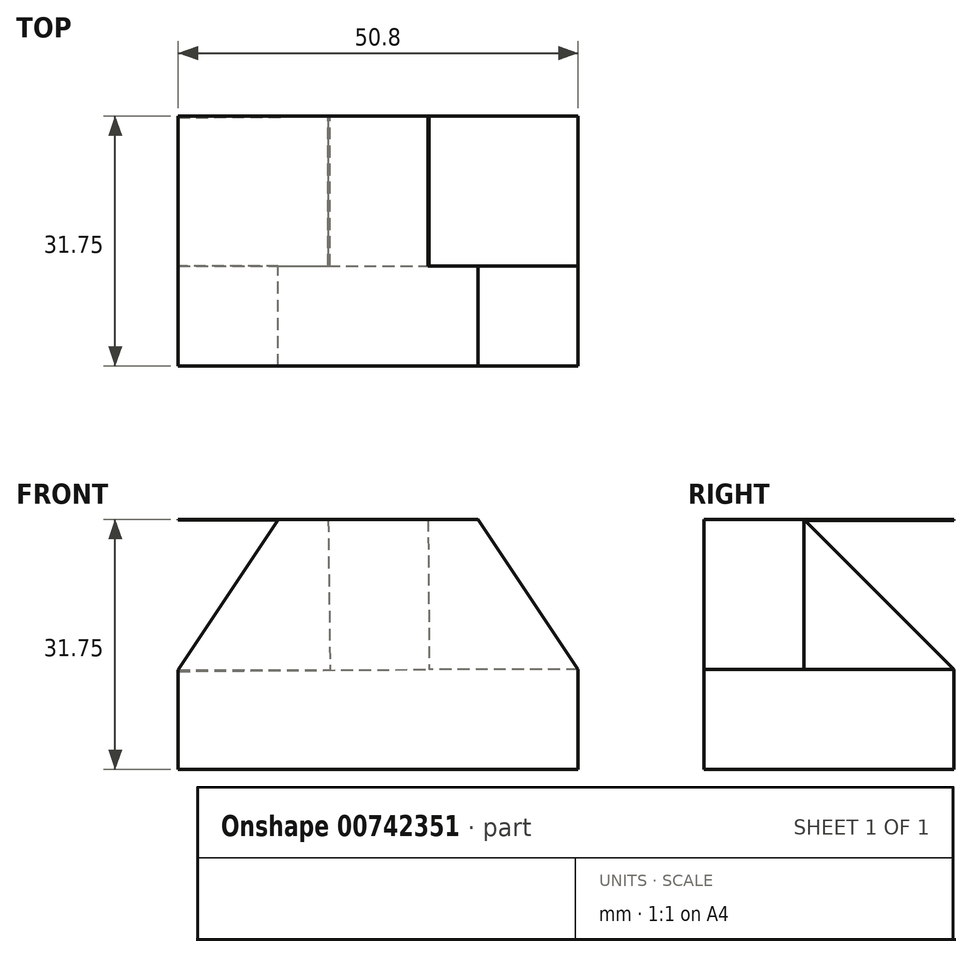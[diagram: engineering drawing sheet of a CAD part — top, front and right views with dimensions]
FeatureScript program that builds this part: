
annotation { "Feature Type Name" : "Feature", "Feature Type Description" : "" }
export const myFeature = defineFeature(function(context is Context, id is Id, definition is map)
    precondition{}
    {
        {
            var Q0;
            Q0=qCreatedBy(makeId("Front.planeOp"),FACE);
            var sketch = newSketch(context, id + "F0", { "sketchPlane" : qUnion([Q0])});
            skLineSegment(sketch, "E0", {"start": v(0, 0) * mm, "end": v(50.8, 0) * mm});
            skLineSegment(sketch, "E1", {"start": v(50.8, 0) * mm, "end": v(50.8, 31.75) * mm});
            skLineSegment(sketch, "E2", {"start": v(50.8, 31.75) * mm, "end": v(0, 31.75) * mm});
            skLineSegment(sketch, "E3", {"start": v(0, 31.75) * mm, "end": v(0, 0) * mm});
            skSolve(sketch);
        }
        {
            var Q0;
            Q0 = qSketchRegion(id + "F0", true);
            extrude(context, id + "F1", {"entities" : qUnion([Q0]), "depth" : 31.75 * mm, "offsetDistance" : 25.4 * mm});
        }
        {
            var Q0;
            Q0=qCreatedBy(makeId("Front.planeOp"),FACE);
            var sketch = newSketch(context, id + "F2", { "sketchPlane" : qUnion([Q0])});
            skLineSegment(sketch, "E4", {"start": v(50.83, 12.7) * mm, "end": v(31.89, 12.7) * mm});
            skLineSegment(sketch, "E5", {"start": v(31.89, 12.7) * mm, "end": v(31.75, 31.75) * mm});
            skLineSegment(sketch, "E6", {"start": v(31.75, 31.75) * mm, "end": v(50.8, 31.75) * mm});
            skLineSegment(sketch, "E7", {"start": v(50.8, 31.75) * mm, "end": v(50.83, 12.7) * mm});
            skLineSegment(sketch, "E8", {"start": v(0, 12.66) * mm, "end": v(19.3, 12.66) * mm});
            skLineSegment(sketch, "E9", {"start": v(0, 12.66) * mm, "end": v(0, 31.71) * mm});
            skLineSegment(sketch, "E10", {"start": v(0, 31.71) * mm, "end": v(19.05, 31.71) * mm});
            skLineSegment(sketch, "E11", {"start": v(19.05, 31.71) * mm, "end": v(19.3, 12.66) * mm});
            skSolve(sketch);
        }
        {
            var Q0;
            Q0 = qSketchRegion(id + "F2", true);
            extrude(context, id + "F3", {"entities" : qUnion([Q0]), "operationType" : NewBodyOperationType.REMOVE, "depth" : 19.05 * mm, "offsetDistance" : 25.4 * mm});
        }
        {
            var Q0;
            Q0=makeQuery(id+"F3.boolean.opBoolean","COPY",FACE,{"derivedFrom":makeQuery(id+"F3.opExtrude","CAP_FACE",FACE,{"disambiguationData":[OSD([sQuery(id+"F2.wireOp",EDGE,"E8"),sQuery(id+"F2.wireOp",EDGE,"E9"),sQuery(id+"F2.wireOp",EDGE,"E10"),sQuery(id+"F2.wireOp",EDGE,"E11")])],"isStart":false})});
            var sketch = newSketch(context, id + "F4", { "sketchPlane" : qUnion([Q0])});
            skLineSegment(sketch, "E12", {"start": v(-12.7, 31.71) * mm, "end": v(0, 12.66) * mm});
            skLineSegment(sketch, "E13", {"start": v(0, 12.66) * mm, "end": v(0, 31.71) * mm});
            skLineSegment(sketch, "E14", {"start": v(0, 31.71) * mm, "end": v(-12.7, 31.71) * mm});
            skSolve(sketch);
        }
        {
            var Q0;
            Q0 = qSketchRegion(id + "F4", true);
            extrude(context, id + "F5", {"entities" : qUnion([Q0]), "operationType" : NewBodyOperationType.REMOVE, "endBound" : BoundingType.THROUGH_ALL, "oppositeDirection" : true, "depth" : 25.4 * mm, "offsetDistance" : 25.4 * mm});
        }
        {
            var Q0;
            Q0=makeQuery(id+"F3.boolean.opBoolean","COPY",FACE,{"derivedFrom":makeQuery(id+"F3.opExtrude","CAP_FACE",FACE,{"disambiguationData":[OSD([sQuery(id+"F2.wireOp",EDGE,"E4"),sQuery(id+"F2.wireOp",EDGE,"E5"),sQuery(id+"F2.wireOp",EDGE,"E6"),sQuery(id+"F2.wireOp",EDGE,"E7")])],"isStart":false})});
            var sketch = newSketch(context, id + "F6", { "sketchPlane" : qUnion([Q0])});
            skLineSegment(sketch, "E15", {"start": v(-50.8, 12.7) * mm, "end": v(-38.1, 31.75) * mm});
            skLineSegment(sketch, "E16", {"start": v(-38.1, 31.75) * mm, "end": v(-50.8, 31.75) * mm});
            skLineSegment(sketch, "E17", {"start": v(-50.8, 31.75) * mm, "end": v(-50.8, 12.7) * mm});
            skSolve(sketch);
        }
        {
            var Q0;
            Q0 = qSketchRegion(id + "F6", true);
            extrude(context, id + "F7", {"entities" : qUnion([Q0]), "operationType" : NewBodyOperationType.REMOVE, "endBound" : BoundingType.THROUGH_ALL, "oppositeDirection" : true, "depth" : 25.4 * mm, "offsetDistance" : 25.4 * mm});
        }
        {
            var Q0;
            Q0=makeQuery(id+"F3.boolean.opBoolean","COPY",FACE,{"derivedFrom":makeQuery(id+"F3.opExtrude","SWEPT_FACE",FACE,{"disambiguationData":[OSD([sQuery(id+"F2.wireOp",EDGE,"E5")])]})});
            var sketch = newSketch(context, id + "F8", { "sketchPlane" : qUnion([Q0])});
            skLineSegment(sketch, "E18", {"start": v(-19.05, 31.52) * mm, "end": v(0, 12.47) * mm});
            skLineSegment(sketch, "E19", {"start": v(0, 12.47) * mm, "end": v(0, 31.52) * mm});
            skLineSegment(sketch, "E20", {"start": v(0, 31.52) * mm, "end": v(-19.05, 31.52) * mm});
            skSolve(sketch);
        }
        {
            var Q0;
            Q0 = qSketchRegion(id + "F8", true);
            extrude(context, id + "F9", {"entities" : qUnion([Q0]), "operationType" : NewBodyOperationType.REMOVE, "endBound" : BoundingType.THROUGH_ALL, "oppositeDirection" : true, "depth" : 25.4 * mm, "offsetDistance" : 25.4 * mm});
        }
    });
